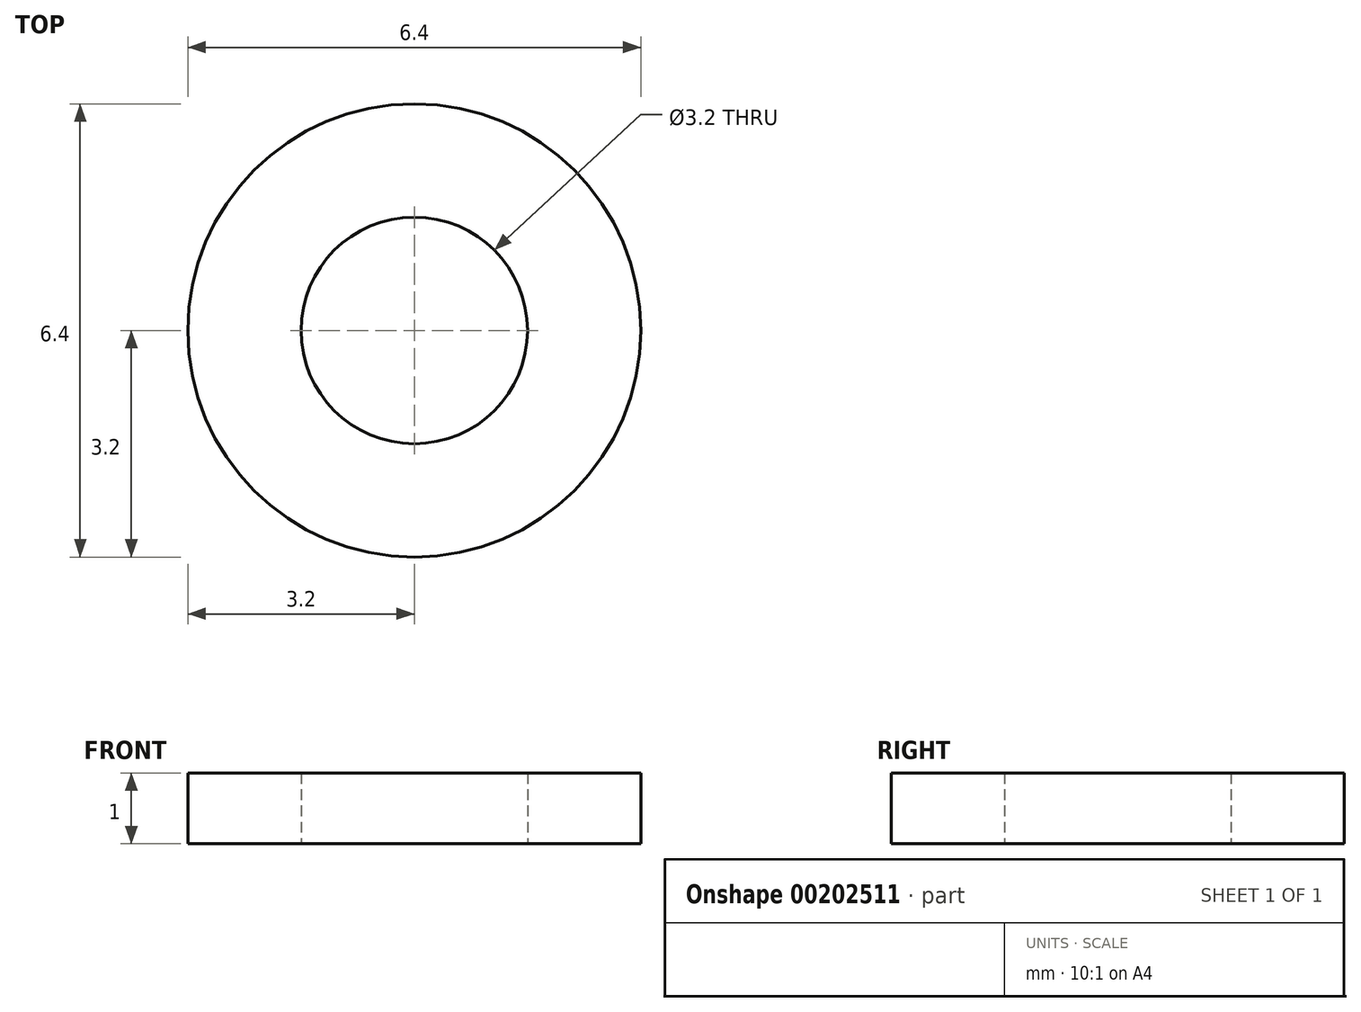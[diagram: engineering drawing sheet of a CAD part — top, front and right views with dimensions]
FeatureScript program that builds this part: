
annotation { "Feature Type Name" : "Feature", "Feature Type Description" : "" }
export const myFeature = defineFeature(function(context is Context, id is Id, definition is map)
    precondition{}
    {
        {
            var Q0;
            Q0=qCreatedBy(makeId("Top.planeOp"),FACE);
            var sketch = newSketch(context, id + "F0", { "sketchPlane" : qUnion([Q0])});
            skCircle(sketch, "E0", {"center": v(0, 0) * mm, "radius": 3.2 * mm});
            skSolve(sketch);
        }
        {
            var Q0;
            Q0=makeQuery(id+"F0.imprint","IMPRINT",FACE,{"disambiguationData":[TD([[makeQuery(id+"F0.imprint","IMPRINT",EDGE,{"derivedFrom":sQuery(id+"F0.wireOp",EDGE,"E0")}),1.0]])]});
            var Q1;
            Q1 = qSketchRegion(id + "F0", true);
            extrude(context, id + "F1", {"entities" : qUnion([Q0, Q1]), "depth" : 1 * mm});
        }
        {
            var Q0;
            Q0=sQuery(id+"F0.wireOp",VERTEX,"E0.center");
            var Q1;
            Q1=makeQuery(id+"F1.opExtrude","SWEPT_BODY",BODY,{"disambiguationData":[OSD([sQuery(id+"F0.wireOp",EDGE,"E0")])]});
            hole(context, id + "F2", {"style" : HoleStyle.SIMPLE, "endStyle" : HoleEndStyle.THROUGH, "oppositeDirection" : true, "holeDiameter" : 3.2 * mm, "locations" : qUnion([Q0]), "scope" : qUnion([Q1]), "isTappedThrough" : true});
        }
    });
